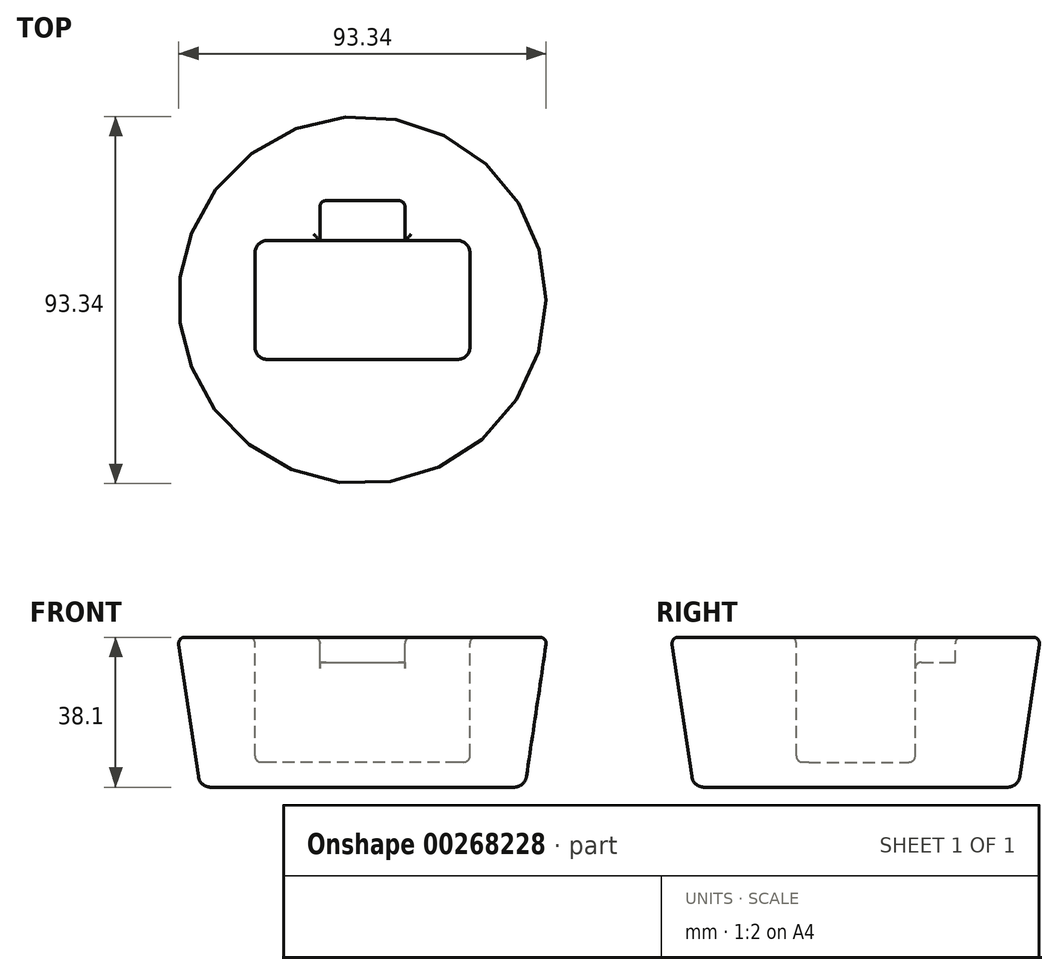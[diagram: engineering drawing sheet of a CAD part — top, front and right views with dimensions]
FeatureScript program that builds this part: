
annotation { "Feature Type Name" : "Feature", "Feature Type Description" : "" }
export const myFeature = defineFeature(function(context is Context, id is Id, definition is map)
    precondition{}
    {
        {
            var Q0;
            Q0=qCreatedBy(makeId("Top.planeOp"),FACE);
            var sketch = newSketch(context, id + "F0", { "sketchPlane" : qUnion([Q0])});
            skCircle(sketch, "E0", {"center": v(0, 0) * mm, "radius": 41.28 * mm});
            skSolve(sketch);
        }
        {
            var Q0;
            Q0=qCreatedBy(makeId("Top.planeOp"),FACE);
            cPlane(context, id + "F1", {"entities" : qUnion([Q0]), "cplaneType" : CPlaneType.OFFSET, "offset" : 83.06 * mm, "width" : 152.4 * mm, "height" : 152.4 * mm});
        }
        {
            var Q0;
            Q0=qCreatedBy(id+"F1.planeOp",FACE);
            var sketch = newSketch(context, id + "F2", { "sketchPlane" : qUnion([Q0])});
            skCircle(sketch, "E1", {"center": v(0, 0) * mm, "radius": 53.6 * mm});
            skSolve(sketch);
        }
        {
            var Q0;
            Q0=makeQuery(id+"F0.imprint","IMPRINT",FACE,{"disambiguationData":[TD([[makeQuery(id+"F0.imprint","IMPRINT",EDGE,{"derivedFrom":sQuery(id+"F0.wireOp",EDGE,"E0")}),1.0]])]});
            var Q1;
            Q1=makeQuery(id+"F2.imprint","IMPRINT",FACE,{"disambiguationData":[TD([[makeQuery(id+"F2.imprint","IMPRINT",EDGE,{"derivedFrom":sQuery(id+"F2.wireOp",EDGE,"E1")}),1.0]])]});
            loft(context, id + "F3", {"sheetProfilesArray" : [{ "sheetProfileEntities" : qUnion([Q0]) }, { "sheetProfileEntities" : qUnion([Q1]) }]});
        }
        {
            var Q0;
            Q0=qCreatedBy(makeId("Top.planeOp"),FACE);
            cPlane(context, id + "F4", {"entities" : qUnion([Q0]), "cplaneType" : CPlaneType.OFFSET, "offset" : 38.1 * mm, "width" : 152.4 * mm, "height" : 152.4 * mm});
        }
        {
            var Q0;
            Q0=makeQuery(id+"F3.opLoft","MID_CAP_EDGE",EDGE,{"disambiguationData":[OSD([sQuery(id+"F0.wireOp",EDGE,"E0")])],"capPos":0.0});
            fillet(context, id + "F5", {"entities" : qUnion([Q0]), "radius" : 3.17 * mm, "tangentPropagation" : true, "allowEdgeOverflow" : false});
        }
        {
            var Q0;
            Q0=qCreatedBy(id+"F4.planeOp",FACE);
            var sketch = newSketch(context, id + "F6", { "sketchPlane" : qUnion([Q0])});
            skLineSegment(sketch, "E2.bottom", {"start": v(24.13, -15.11) * mm, "end": v(-24.13, -15.11) * mm});
            skLineSegment(sketch, "E2.top", {"start": v(24.13, 15.11) * mm, "end": v(-24.13, 15.11) * mm});
            skLineSegment(sketch, "E2.left", {"start": v(27.3, -11.94) * mm, "end": v(27.3, 11.94) * mm});
            skLineSegment(sketch, "E2.right", {"start": v(-27.3, -11.94) * mm, "end": v(-27.3, 11.94) * mm});
            skPoint(sketch, "E2.middle", {"position": v(0, 0) * mm});
            skPoint(sketch, "E3.visualSharp", {"position": v(-27.3, -15.11) * mm});
            skArc(sketch, "E3.filletArc", {"start": v(-27.3, -11.94) * mm, "mid": v(-26.38, -14.18) * mm, "end": v(-24.13, -15.11) * mm});
            skPoint(sketch, "E4.visualSharp", {"position": v(27.3, -15.11) * mm});
            skArc(sketch, "E4.filletArc", {"start": v(24.13, -15.11) * mm, "mid": v(26.38, -14.18) * mm, "end": v(27.3, -11.94) * mm});
            skPoint(sketch, "E5.visualSharp", {"position": v(27.3, 15.11) * mm});
            skArc(sketch, "E5.filletArc", {"start": v(27.3, 11.94) * mm, "mid": v(26.38, 14.18) * mm, "end": v(24.13, 15.11) * mm});
            skPoint(sketch, "E6.visualSharp", {"position": v(-27.3, 15.11) * mm});
            skArc(sketch, "E6.filletArc", {"start": v(-24.13, 15.11) * mm, "mid": v(-26.38, 14.18) * mm, "end": v(-27.3, 11.94) * mm});
            skLineSegment(sketch, "E7", {"start": v(0, 15.11) * mm, "end": v(0, -15.11) * mm});
            skLineSegment(sketch, "E8.bottom", {"start": v(-10.8, 15.11) * mm, "end": v(10.8, 15.11) * mm});
            skLineSegment(sketch, "E8.top", {"start": v(-9.2, 25.27) * mm, "end": v(9.2, 25.27) * mm});
            skLineSegment(sketch, "E8.left", {"start": v(-10.8, 15.11) * mm, "end": v(-10.8, 23.69) * mm});
            skLineSegment(sketch, "E8.right", {"start": v(10.8, 15.11) * mm, "end": v(10.8, 23.69) * mm});
            skPoint(sketch, "E9.visualSharp", {"position": v(-10.8, 25.27) * mm});
            skArc(sketch, "E9.filletArc", {"start": v(-9.2, 25.27) * mm, "mid": v(-10.33, 24.8) * mm, "end": v(-10.8, 23.69) * mm});
            skPoint(sketch, "E10.visualSharp", {"position": v(10.8, 25.27) * mm});
            skArc(sketch, "E10.filletArc", {"start": v(10.8, 23.69) * mm, "mid": v(10.33, 24.8) * mm, "end": v(9.2, 25.27) * mm});
            skSolve(sketch);
        }
        {
            var Q0;
            Q0=makeQuery(id+"F3.opLoft","CAP_FACE",FACE,{"disambiguationData":[OSD([makeQuery(id+"F2.imprint","IMPRINT",FACE,{"disambiguationData":[TD([[makeQuery(id+"F2.imprint","IMPRINT",EDGE,{"derivedFrom":sQuery(id+"F2.wireOp",EDGE,"E1")}),1.0]])]})])],"isStart":true});
            var Q1;
            Q1=qCreatedBy(id+"F4.planeOp",FACE);
            extrude(context, id + "F7", {"entities" : qUnion([Q0]), "operationType" : NewBodyOperationType.REMOVE, "endBound" : BoundingType.UP_TO_SURFACE, "oppositeDirection" : true, "endBoundEntityFace" : qUnion([Q1]), "depth" : 25.4 * mm});
        }
        {
            var Q0;
            Q0=makeQuery(id+"F6.imprint","IMPRINT",FACE,{"disambiguationData":[TD([[makeQuery(id+"F6.imprint","IMPRINT",EDGE,{"derivedFrom":sQuery(id+"F6.wireOp",EDGE,"E2.right")}),-1.0]])]});
            var Q1;
            Q1=makeQuery(id+"F6.imprint","IMPRINT",FACE,{"disambiguationData":[TD([[makeQuery(id+"F6.imprint","IMPRINT",EDGE,{"derivedFrom":sQuery(id+"F6.wireOp",EDGE,"E2.left")}),1.0]])]});
            extrude(context, id + "F8", {"entities" : qUnion([Q0, Q1]), "operationType" : NewBodyOperationType.REMOVE, "oppositeDirection" : true, "depth" : 31.75 * mm});
        }
        {
            var Q0;
            Q0 = qSketchRegion(id + "F6", true);
            extrude(context, id + "F9", {"entities" : qUnion([Q0]), "operationType" : NewBodyOperationType.REMOVE, "oppositeDirection" : true, "depth" : 6.35 * mm});
        }
        {
            var Q0;
            {var subQ0=sQuery(id+"F6.wireOp",EDGE,"E2.top");Q0=makeQuery(id+"F9.boolean.opBoolean","INTERSECT",EDGE,{"derivedFrom":[makeQuery(id+"F8.boolean.opBoolean","COPY",FACE,{"derivedFrom":makeQuery(id+"F8.opExtrude","SWEPT_FACE",FACE,{"disambiguationData":[OSD([subQ0,sQuery(id+"F6.wireOp",EDGE,"E8.bottom")])]})}),makeQuery(id+"F9.opExtrude","CAP_FACE",FACE,{"disambiguationData":[OSD([sQuery(id+"F6.wireOp",EDGE,"E2.bottom"),subQ0,sQuery(id+"F6.wireOp",EDGE,"E2.left"),sQuery(id+"F6.wireOp",EDGE,"E2.right"),sQuery(id+"F6.wireOp",EDGE,"E3.filletArc"),sQuery(id+"F6.wireOp",EDGE,"E4.filletArc"),sQuery(id+"F6.wireOp",EDGE,"E5.filletArc"),sQuery(id+"F6.wireOp",EDGE,"E6.filletArc"),sQuery(id+"F6.wireOp",EDGE,"E8.top"),sQuery(id+"F6.wireOp",EDGE,"E8.left"),sQuery(id+"F6.wireOp",EDGE,"E8.right"),sQuery(id+"F6.wireOp",EDGE,"E9.filletArc"),sQuery(id+"F6.wireOp",EDGE,"E10.filletArc")])],"isStart":false})]});}
            var Q1;
            Q1=makeQuery(id+"F8.boolean.opBoolean","COPY",FACE,{"derivedFrom":makeQuery(id+"F8.opExtrude","CAP_FACE",FACE,{"disambiguationData":[OSD([sQuery(id+"F6.wireOp",EDGE,"E2.bottom"),sQuery(id+"F6.wireOp",EDGE,"E2.top"),sQuery(id+"F6.wireOp",EDGE,"E2.left"),sQuery(id+"F6.wireOp",EDGE,"E2.right"),sQuery(id+"F6.wireOp",EDGE,"E3.filletArc"),sQuery(id+"F6.wireOp",EDGE,"E4.filletArc"),sQuery(id+"F6.wireOp",EDGE,"E5.filletArc"),sQuery(id+"F6.wireOp",EDGE,"E6.filletArc"),sQuery(id+"F6.wireOp",EDGE,"E8.bottom")])],"isStart":false})});
            var Q2;
            Q2=makeQuery(id+"F7.boolean.opBoolean","COPY",FACE,{"derivedFrom":makeQuery(id+"F7.opExtrude","CAP_FACE",FACE,{"disambiguationData":[OSD([makeQuery(id+"F2.imprint","IMPRINT",FACE,{"disambiguationData":[TD([[makeQuery(id+"F2.imprint","IMPRINT",EDGE,{"derivedFrom":sQuery(id+"F2.wireOp",EDGE,"E1")}),1.0]])]})])],"isStart":false})});
            fillet(context, id + "F10", {"entities" : qUnion([Q0, Q1, Q2]), "radius" : 1.59 * mm, "allowEdgeOverflow" : false});
        }
    });
